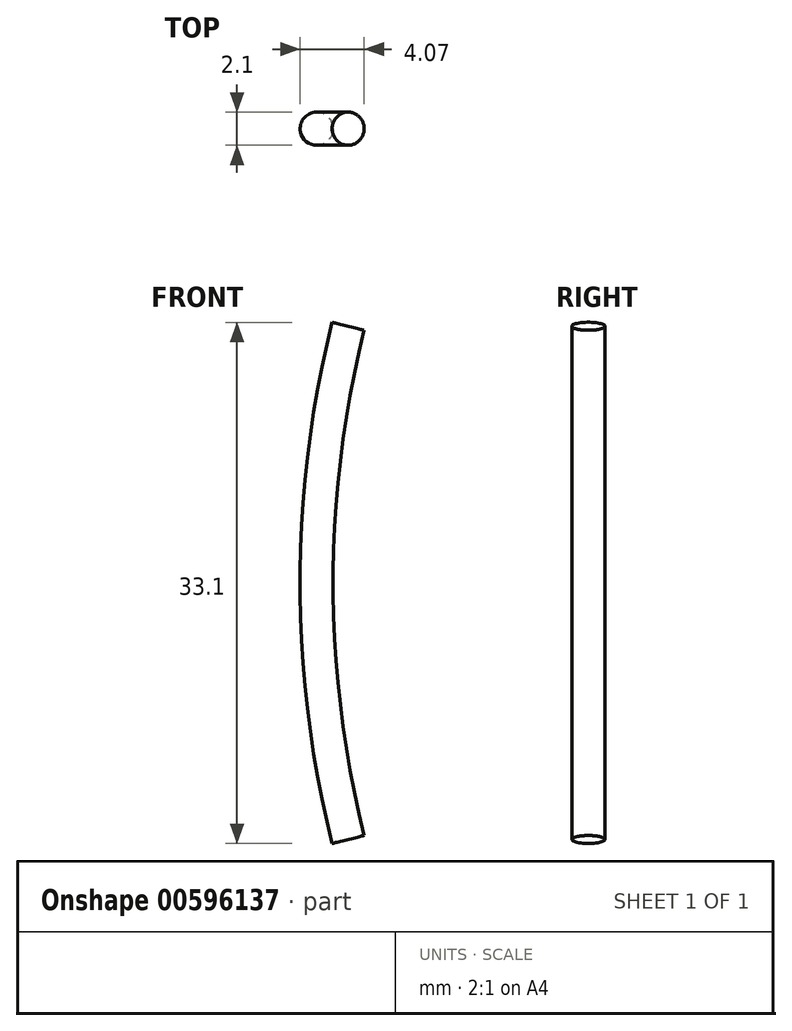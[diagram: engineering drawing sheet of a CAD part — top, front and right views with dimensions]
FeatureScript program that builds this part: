
annotation { "Feature Type Name" : "Feature", "Feature Type Description" : "" }
export const myFeature = defineFeature(function(context is Context, id is Id, definition is map)
    precondition{}
    {
        {
            var Q0;
            Q0=qCreatedBy(makeId("Front.planeOp"),FACE);
            var sketch = newSketch(context, id + "F0", { "sketchPlane" : qUnion([Q0])});
            skLineSegment(sketch, "E0", {"start": v(0, 0) * mm, "end": v(0, 16.3) * mm, "construction": true});
            skLineSegment(sketch, "E1", {"start": v(0, 0) * mm, "end": v(0, -16.3) * mm, "construction": true});
            skLineSegment(sketch, "E2", {"start": v(0, 0) * mm, "end": v(-2, 0) * mm, "construction": true});
            skArc(sketch, "E3", {"start": v(0, 16.3) * mm, "mid": v(-2, 0) * mm, "end": v(0, -16.3) * mm});
            skSolve(sketch);
        }
        {
            var Q0;
            Q0=qCreatedBy(makeId("Top.planeOp"),FACE);
            var sketch = newSketch(context, id + "F1", { "sketchPlane" : qUnion([Q0])});
            skPoint(sketch, "E4.0", {"position": v(-2, 0) * mm});
            skCircle(sketch, "E5", {"center": v(-2, 0) * mm, "radius": 1.05 * mm});
            skSolve(sketch);
        }
        {
            var Q0;
            Q0=makeQuery(id+"F1.imprint","IMPRINT",FACE,{"disambiguationData":[TD([[makeQuery(id+"F1.imprint","IMPRINT",EDGE,{"derivedFrom":sQuery(id+"F1.wireOp",EDGE,"E5")}),1.0]])]});
            var Q1;
            Q1=sQuery(id+"F0.wireOp",EDGE,"E3");
            sweep(context, id + "F2", {"profiles" : qUnion([Q0]), "path" : qUnion([Q1])});
        }
    });
